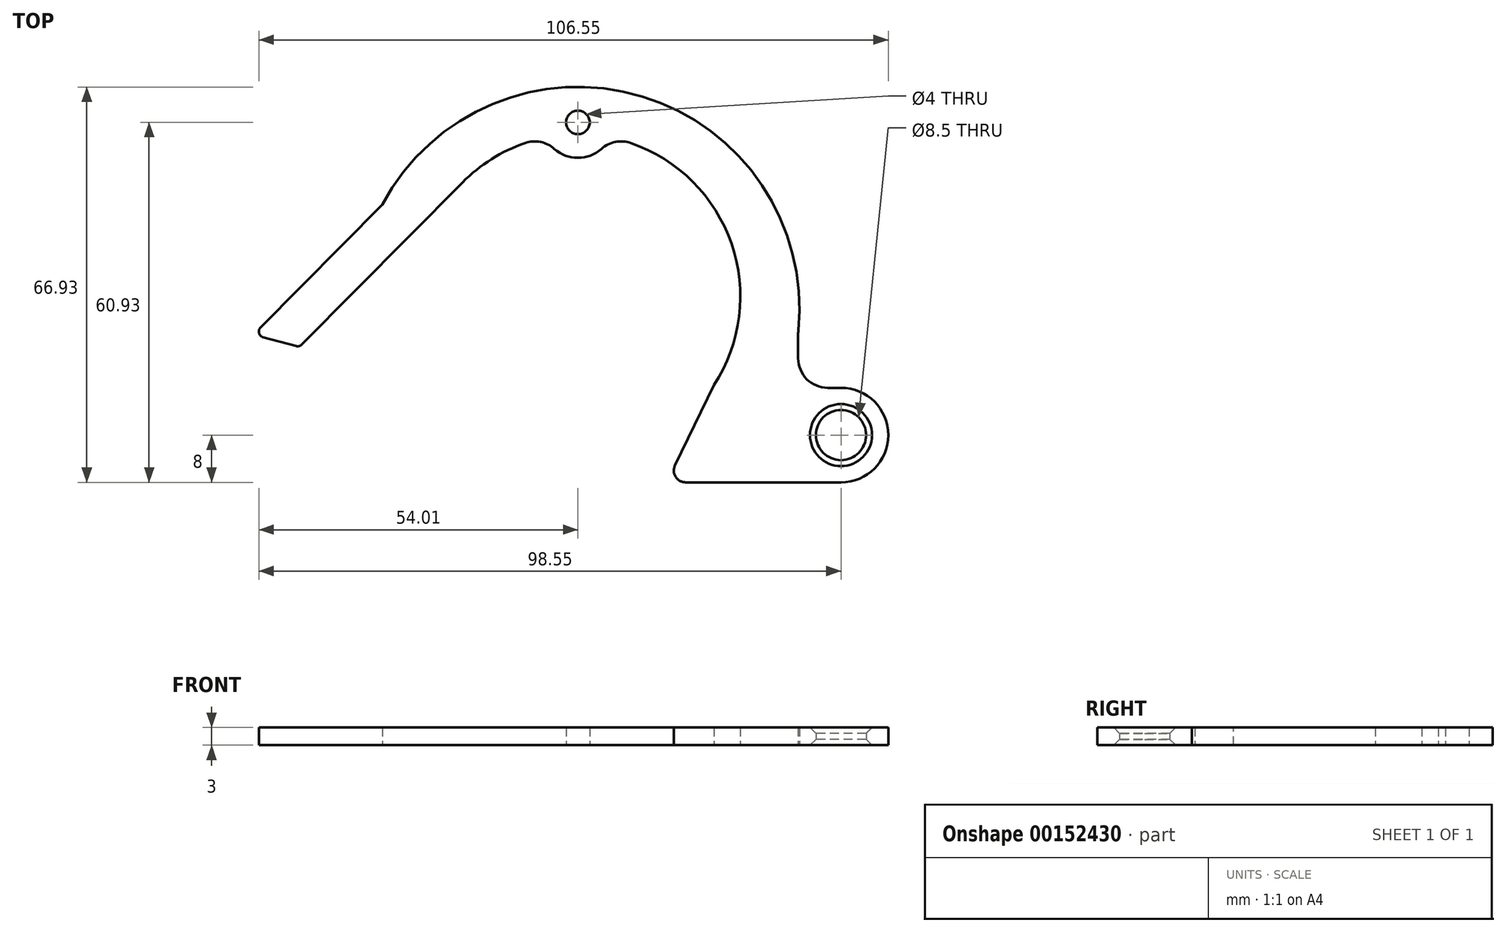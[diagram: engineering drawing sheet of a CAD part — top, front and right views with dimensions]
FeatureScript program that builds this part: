
annotation { "Feature Type Name" : "Feature", "Feature Type Description" : "" }
export const myFeature = defineFeature(function(context is Context, id is Id, definition is map)
    precondition{}
    {
        {
            var Q0;
            Q0=qCreatedBy(makeId("Top.planeOp"),FACE);
            var sketch = newSketch(context, id + "F0", { "sketchPlane" : qUnion([Q0])});
            skLineSegment(sketch, "E0", {"start": v(3.2, 0) * mm, "end": v(29.5, 0) * mm});
            skArc(sketch, "E1", {"start": v(29.5, 0) * mm, "mid": v(37.5, 8) * mm, "end": v(29.5, 16) * mm});
            skCircle(sketch, "E2", {"center": v(29.5, 8) * mm, "radius": 4.25 * mm});
            skLineSegment(sketch, "E3", {"start": v(29.5, 8) * mm, "end": v(29.5, 16) * mm, "construction": true});
            skLineSegment(sketch, "E4", {"start": v(1.4, 2.88) * mm, "end": v(10.96, 22.47) * mm});
            skPoint(sketch, "E5.visualSharp", {"position": v(0, 0) * mm});
            skArc(sketch, "E5.filletArc", {"start": v(1.4, 2.88) * mm, "mid": v(1.5, 0.94) * mm, "end": v(3.2, 0) * mm});
            skLineSegment(sketch, "E6", {"start": v(1.4, 2.88) * mm, "end": v(0, 0) * mm, "construction": true});
            skPoint(sketch, "E7", {"position": v(10.96, 22.47) * mm});
            skPoint(sketch, "E8", {"position": v(37.5, 8) * mm});
            skLineSegment(sketch, "E9", {"start": v(22.25, 22.4) * mm, "end": v(22.25, 25.47) * mm});
            skPoint(sketch, "E10", {"position": v(25.25, 8) * mm});
            skLineSegment(sketch, "E11", {"start": v(25.25, 15.56) * mm, "end": v(25.25, 16) * mm, "construction": true});
            skLineSegment(sketch, "E12", {"start": v(0, 0) * mm, "end": v(-48.4, 46.77) * mm, "construction": true});
            skPoint(sketch, "E13", {"position": v(-48.4, 46.77) * mm});
            skLineSegment(sketch, "E14", {"start": v(-48.4, 46.77) * mm, "end": v(-40.62, 44.68) * mm, "construction": true});
            skLineSegment(sketch, "E15", {"start": v(-40.62, 44.68) * mm, "end": v(-19.23, 44.68) * mm, "construction": true});
            skLineSegment(sketch, "E16", {"start": v(-40.62, 44.68) * mm, "end": v(-54.62, 44.68) * mm, "construction": true});
            skLineSegment(sketch, "E17", {"start": v(-48.16, 47.02) * mm, "end": v(-69.97, 25) * mm});
            skLineSegment(sketch, "E18", {"start": v(-69.97, 25) * mm, "end": v(-62.19, 22.9) * mm});
            skLineSegment(sketch, "E19", {"start": v(-34.58, 50.78) * mm, "end": v(-62.19, 22.9) * mm});
            skLineSegment(sketch, "E20", {"start": v(29.5, 16) * mm, "end": v(27.25, 16) * mm});
            skPoint(sketch, "E21.orphan", {"position": v(22.25, 15.4) * mm});
            skPoint(sketch, "E22.endSnap0", {"position": v(-5.81, -11.91) * mm});
            skPoint(sketch, "E23.orphan", {"position": v(-11.62, -23.83) * mm});
            skPoint(sketch, "E22.start.orphan", {"position": v(-30.24, 0) * mm});
            skPoint(sketch, "E24", {"position": v(21.45, 16.47) * mm});
            skLineSegment(sketch, "E25", {"start": v(10.6, 21.76) * mm, "end": v(10.61, 21.76) * mm, "construction": true});
            skPoint(sketch, "E26.end.orphan", {"position": v(32.88, 67.4) * mm});
            skLineSegment(sketch, "E27", {"start": v(22.25, 21) * mm, "end": v(22.25, 67.68) * mm, "construction": true});
            skCircle(sketch, "E28", {"center": v(-15.04, 60.93) * mm, "radius": 2 * mm});
            skCircle(sketch, "E29", {"center": v(-15.04, 60.93) * mm, "radius": 6 * mm});
            skLineSegment(sketch, "E30", {"start": v(-15.04, 66.93) * mm, "end": v(-15.04, 31.43) * mm, "construction": true});
            skCircle(sketch, "E31", {"center": v(-15.04, 29.43) * mm, "radius": 37.5 * mm});
            skCircle(sketch, "E32", {"center": v(-15.04, 31.43) * mm, "radius": 27.5 * mm});
            skPoint(sketch, "E33.visualSharp", {"position": v(22.25, 16) * mm});
            skArc(sketch, "E33.filletArc", {"start": v(22.25, 21) * mm, "mid": v(23.71, 17.46) * mm, "end": v(27.25, 16) * mm});
            skLineSegment(sketch, "E34", {"start": v(22.25, 21) * mm, "end": v(22.25, 22.4) * mm});
            skSolve(sketch);
        }
        {
            var Q0;
            {var subQ0=sQuery(id+"F0.wireOp",EDGE,"E17");Q0=makeQuery(id+"F0.imprint","IMPRINT",FACE,{"disambiguationData":[TD([[makeQuery(id+"F0.imprint","IMPRINT",EDGE,{"derivedFrom":subQ0}),1.0]])]});}
            var Q1;
            {var subQ2=sQuery(id+"F0.wireOp",EDGE,"E19");var subQ6=sQuery(id+"F0.wireOp",EDGE,"E32");var subQ8=makeQuery(id+"F0.imprint","INTERSECT",VERTEX,{"derivedFrom":[subQ2,subQ6]});Q1=makeQuery(id+"F0.imprint","IMPRINT",FACE,{"disambiguationData":[TD([[makeQuery(id+"F0.imprint","IMPRINT",EDGE,{"disambiguationData":[TD([[subQ8,-1.0]])],"derivedFrom":subQ2}),-1.0]])]});}
            var Q2;
            {var subQ1=sQuery(id+"F0.wireOp",EDGE,"E28");Q2=makeQuery(id+"F0.imprint","IMPRINT",FACE,{"disambiguationData":[TD([[makeQuery(id+"F0.imprint","IMPRINT",EDGE,{"derivedFrom":subQ1}),-1.0]])]});}
            var Q3;
            {var subQ0=sQuery(id+"F0.wireOp",EDGE,"E32");var subQ1=sQuery(id+"F0.wireOp",EDGE,"E29");var subQ2=makeQuery(id+"F0.imprint","INTERSECT",VERTEX,{"disambiguationData":[OD(0.0)],"derivedFrom":[subQ1,subQ0]});Q3=makeQuery(id+"F0.imprint","IMPRINT",FACE,{"disambiguationData":[TD([[makeQuery(id+"F0.imprint","IMPRINT",EDGE,{"disambiguationData":[TD([[subQ2,-1.0]])],"derivedFrom":subQ1}),1.0]])]});}
            var Q4;
            {var subQ0=sQuery(id+"F0.wireOp",EDGE,"E5.filletArc");Q4=makeQuery(id+"F0.imprint","IMPRINT",FACE,{"disambiguationData":[TD([[makeQuery(id+"F0.imprint","IMPRINT",EDGE,{"derivedFrom":subQ0}),1.0]])]});}
            var Q5;
            {var subQ1=sQuery(id+"F0.wireOp",EDGE,"E1");Q5=makeQuery(id+"F0.imprint","IMPRINT",FACE,{"disambiguationData":[TD([[makeQuery(id+"F0.imprint","IMPRINT",EDGE,{"derivedFrom":subQ1}),1.0]])]});}
            extrude(context, id + "F1", {"entities" : qUnion([Q0, Q1, Q2, Q3, Q4, Q5]), "depth" : 3 * mm});
        }
        {
            var Q0;
            {var subQ0=sQuery(id+"F0.wireOp",EDGE,"E32");var subQ1=sQuery(id+"F0.wireOp",EDGE,"E29");Q0=makeQuery(id+"F1.opExtrude","SWEPT_EDGE",EDGE,{"disambiguationData":[OSD([subQ1,subQ0]),TDD([makeQuery(id+"F0.imprint","INTERSECT",VERTEX,{"disambiguationData":[OD(0.0)],"derivedFrom":[subQ1,subQ0]})])]});}
            var Q1;
            {var subQ0=sQuery(id+"F0.wireOp",EDGE,"E32");var subQ1=sQuery(id+"F0.wireOp",EDGE,"E29");Q1=makeQuery(id+"F1.opExtrude","SWEPT_EDGE",EDGE,{"disambiguationData":[OSD([subQ1,subQ0]),TDD([makeQuery(id+"F0.imprint","INTERSECT",VERTEX,{"disambiguationData":[OD(1.0)],"derivedFrom":[subQ1,subQ0]})])]});}
            fillet(context, id + "F2", {"entities" : qUnion([Q0, Q1]), "radius" : 5 * mm, "tangentPropagation" : true, "allowEdgeOverflow" : false});
        }
        {
            var Q0;
            Q0=makeQuery(id+"F1.opExtrude","SWEPT_EDGE",EDGE,{"disambiguationData":[OSD([sQuery(id+"F0.wireOp",EDGE,"1qSlrM0i-sSkW-lbLZ-bidS-qWem4HMrsFkF"),sQuery(id+"F0.wireOp",EDGE,"E9")])]});
            var Q1;
            Q1=makeQuery(id+"F1.opExtrude","SWEPT_EDGE",EDGE,{"disambiguationData":[OSD([sQuery(id+"F0.wireOp",EDGE,"vIPYT7S5-gq9l-VRMR-vKiI-8soHfzf1ns7e"),sQuery(id+"F0.wireOp",EDGE,"E9")])]});
            fillet(context, id + "F3", {"entities" : qUnion([Q0, Q1]), "radius" : 6 * mm, "tangentPropagation" : true, "allowEdgeOverflow" : false});
        }
        {
            var Q0;
            Q0=makeQuery(id+"F1.opExtrude","SWEPT_EDGE",EDGE,{"disambiguationData":[OSD([sQuery(id+"F0.wireOp",EDGE,"E17"),sQuery(id+"F0.wireOp",EDGE,"E18")])]});
            var Q1;
            Q1=makeQuery(id+"F1.opExtrude","SWEPT_EDGE",EDGE,{"disambiguationData":[OSD([sQuery(id+"F0.wireOp",EDGE,"E18"),sQuery(id+"F0.wireOp",EDGE,"E19")])]});
            fillet(context, id + "F4", {"entities" : qUnion([Q0, Q1]), "radius" : 1 * mm, "tangentPropagation" : true, "allowEdgeOverflow" : false});
        }
        {
            var Q0;
            Q0=makeQuery(id+"F1.opExtrude","CAP_EDGE",EDGE,{"disambiguationData":[OSD([sQuery(id+"F0.wireOp",EDGE,"E2")])],"isStart":false});
            var Q1;
            Q1=makeQuery(id+"F1.opExtrude","CAP_EDGE",EDGE,{"disambiguationData":[OSD([sQuery(id+"F0.wireOp",EDGE,"E2")])],"isStart":true});
            chamfer(context, id + "F5", {"entities" : qUnion([Q0, Q1]), "width" : 1 * mm, "tangentPropagation" : true});
        }
    });
